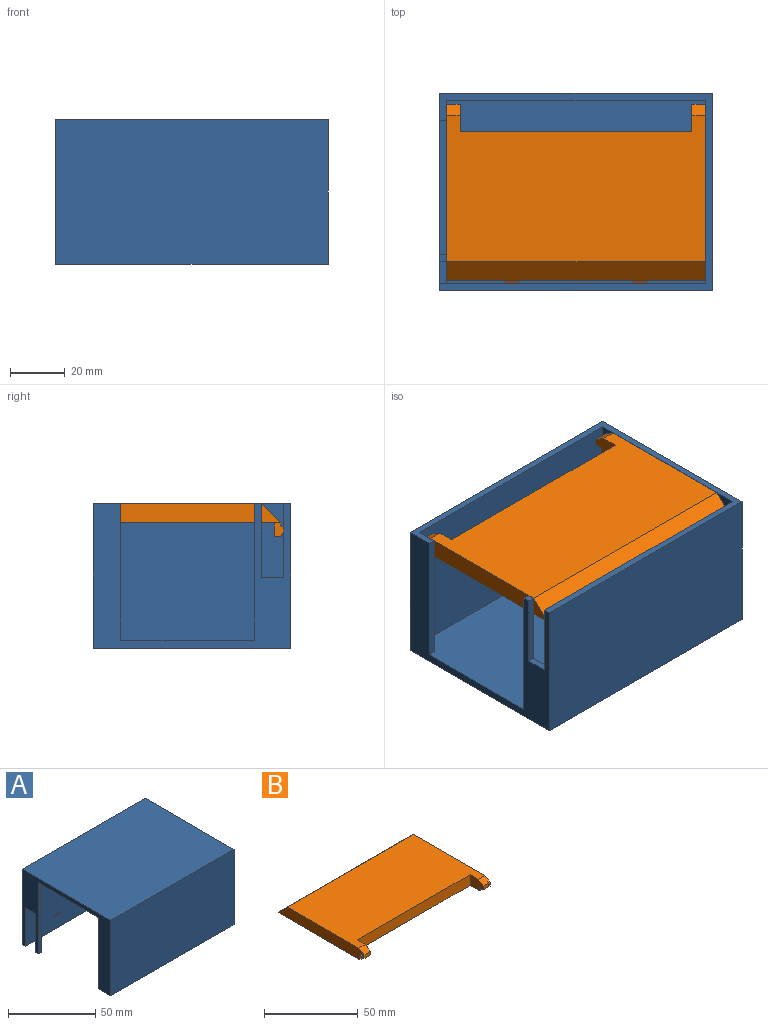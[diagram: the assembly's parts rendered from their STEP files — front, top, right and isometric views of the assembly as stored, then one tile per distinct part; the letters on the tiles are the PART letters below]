
ASSEMBLY  parts=2 mates=1
PART A: 29 faces, bbox 100x72.3x53 mm
  f0: plane 97.5x50mm, normal (0,-1,0), area 4804.2mm2, adj f1,f2,f4,f6,f7,f14,f21,f22
  f1: plane 8.19x2.5mm, normal (0,0,-1), area 20.5mm2, adj f0,f6,f14,f15
  f2: plane 97.5x67.3mm, normal (0,0,-1), area 6516.3mm2, adj f0,f3,f4,f6,f11,f12,f13,f14
  f3: plane 95x50mm, normal (0,1,0), area 4750mm2, adj f2,f4,f7,f12
  f4: plane 67.3x50mm, normal (-1,0,0), area 3360.5mm2, adj f0,f2,f3,f7,f19
  f5: plane 100x72.3mm, normal (0,0,1), area 7230mm2, adj f6,f8,f9,f10
  f6: plane 72.3x53mm, normal (-1,0,0), area 1155.3mm2, adj f0,f1,f2,f5,f7,f9,f10,f11
  f7: plane 100x72.3mm, normal (0,0,-1), area 687mm2, adj f0,f3,f4,f6,f8,f9,f10,f11
  f8: plane 72.3x53mm, normal (1,0,0), area 3831.9mm2, adj f5,f7,f9,f10
  f9: plane 100x53mm, normal (0,-1,0), area 5300mm2, adj f5,f6,f7,f8
  f10: plane 100x53mm, normal (0,1,0), area 5300mm2, adj f5,f6,f7,f8
  f11: plane 50x2.5mm, normal (0,1,0), area 125mm2, adj f2,f6,f7,f12
  f12: plane 50x7.5mm, normal (1,0,0), area 370.5mm2, adj f2,f3,f7,f11,f17
  f13: plane 50x2.5mm, normal (0,-1,0), area 125mm2, adj f2,f6,f14,f16
  f14: plane 50x10.69mm, normal (1,0,0), area 313.4mm2, adj f0,f1,f2,f13,f15,f16
  f15: plane 27x2.5mm, normal (0,1,0), area 67.5mm2, adj f1,f6,f14,f16
  f16: plane 2.5x2.5mm, normal (0,0,-1), area 6.2mm2, adj f6,f13,f14,f15
  f17: cylinder r=1.2mm len=2.4mm, axis (-1,0,0), area 7.5mm2, adj f12,f18
  f18: plane 2.4x2.4mm, normal (1,0,0), area 4.5mm2, adj f17
  f19: cylinder r=1.2mm len=2.4mm, axis (1,0,0), area 7.5mm2, adj f4,f20
  f20: plane 2.4x2.4mm, normal (-1,0,0), area 4.5mm2, adj f19
  f21: plane 5x1mm, normal (0,-0.89,-0.45), area 5.6mm2, adj f0,f22,f23,f24
  f22: plane 5x0.5mm, normal (0,-0.55,0.83), area 3mm2, adj f0,f21,f23,f24
  f23: plane 1.33x0.5mm, normal (-1,0,0), area 0.3mm2, adj f0,f21,f22
  f24: plane 1.33x0.5mm, normal (1,0,0), area 0.3mm2, adj f0,f21,f22
  f25: plane 1.33x0.5mm, normal (1,0,0), area 0.3mm2, adj f0,f27,f28
  f26: plane 1.33x0.5mm, normal (-1,0,0), area 0.3mm2, adj f0,f27,f28
  f27: plane 5x1mm, normal (0,-0.89,-0.45), area 5.6mm2, adj f0,f25,f26,f28
  f28: plane 5x0.5mm, normal (0,-0.55,0.83), area 3mm2, adj f0,f25,f26,f27
PART B: 33 faces, bbox 95x66.3x12 mm
  f0: plane 95x53.72mm, normal (0,0,1), area 4593.6mm2, adj f5,f6,f7,f8,f9,f18,f19,f32
  f1: plane 95x1.17mm, normal (0,1,0), area 25.9mm2, adj f4,f5,f7,f20,f22,f24,f26,f29
  f2: plane 5x2.45mm, normal (0,-1,0), area 12.2mm2, adj f7,f9,f17,f19
  f3: plane 5x2.45mm, normal (0,-1,0), area 12.2mm2, adj f5,f6,f14,f18
  f4: plane 95x61.8mm, normal (0,0,-1), area 5251mm2, adj f1,f5,f6,f7,f8,f9,f15,f16
  f5: plane 64.8x7mm, normal (-1,0,0), area 413.3mm2, adj f0,f1,f3,f4,f10,f14,f15,f18
  f6: plane 10x7mm, normal (1,0,0), area 58.8mm2, adj f0,f3,f4,f8,f14,f15,f18
  f7: plane 64.8x7mm, normal (1,0,0), area 413.3mm2, adj f0,f1,f2,f4,f12,f16,f17,f19
  f8: plane 85x7mm, normal (0,-1,0), area 595mm2, adj f0,f4,f6,f9
  f9: plane 10x7mm, normal (-1,0,0), area 58.8mm2, adj f0,f2,f4,f8,f16,f17,f19
  f10: cylinder r=1.25mm len=2.5mm, axis (-1,0,0), area 7.9mm2, adj f5,f11
  f11: plane 2.5x2.5mm, normal (-1,0,0), area 4.9mm2, adj f10
  f12: cylinder r=1.25mm len=2.5mm, axis (1,0,0), area 7.9mm2, adj f7,f13
  f13: plane 2.5x2.5mm, normal (1,0,0), area 4.9mm2, adj f12
  f14: plane 5x3mm, normal (0,0,-1), area 15mm2, adj f3,f5,f6,f15
  f15: plane 5x2.1mm, normal (0,-1,0), area 10.5mm2, adj f4,f5,f6,f14
  f16: plane 5x2.1mm, normal (0,-1,0), area 10.5mm2, adj f4,f7,f9,f17
  f17: plane 5x3mm, normal (0,0,-1), area 15mm2, adj f2,f7,f9,f16
  f18: plane 5x4mm, normal (0,-0.52,0.85), area 23.5mm2, adj f0,f3,f5,f6
  f19: plane 5x4mm, normal (0,-0.52,0.85), area 23.5mm2, adj f0,f2,f7,f9
  f20: plane 5x4mm, normal (1,0,0), area 15.5mm2, adj f1,f4,f21,f23,f28,f29
  f21: plane 5x5mm, normal (0,-1,0), area 25mm2, adj f4,f20,f22,f23
  f22: plane 5x4mm, normal (-1,0,0), area 15.5mm2, adj f1,f4,f21,f23,f28,f29
  f23: plane 5x2.5mm, normal (0,0,-1), area 12.5mm2, adj f20,f21,f22,f28
  f24: plane 5x4mm, normal (1,0,0), area 15.5mm2, adj f1,f4,f25,f27,f30,f31
  f25: plane 5x5mm, normal (0,-1,0), area 25mm2, adj f4,f24,f26,f27
  f26: plane 5x4mm, normal (-1,0,0), area 15.5mm2, adj f1,f4,f25,f27,f30,f31
  f27: plane 5x2.5mm, normal (0,0,-1), area 12.5mm2, adj f24,f25,f26,f31
  f28: plane 5x3mm, normal (0,0.89,-0.45), area 16.8mm2, adj f20,f22,f23,f29
  f29: plane 5x1.5mm, normal (0,0.55,0.83), area 9mm2, adj f1,f20,f22,f28
  f30: plane 5x1.5mm, normal (0,0.55,0.83), area 9mm2, adj f1,f24,f26,f31
  f31: plane 5x3mm, normal (0,0.89,-0.45), area 16.8mm2, adj f24,f26,f27,f30
  f32: plane 95x7.08mm, normal (0,0.69,0.72), area 934.6mm2, adj f0,f1,f5,f7
PLACE A rot(axis=(1,0,0),180deg) t=(0,33.65,26.5)mm fixed
PLACE B rot(axis=(0,0,-1),180deg) t=(0,-5.25,46)mm
MATE revolute B.f12 <-> A.f17  axis (-1,0,0) through (0,30.65,49.5)mm
